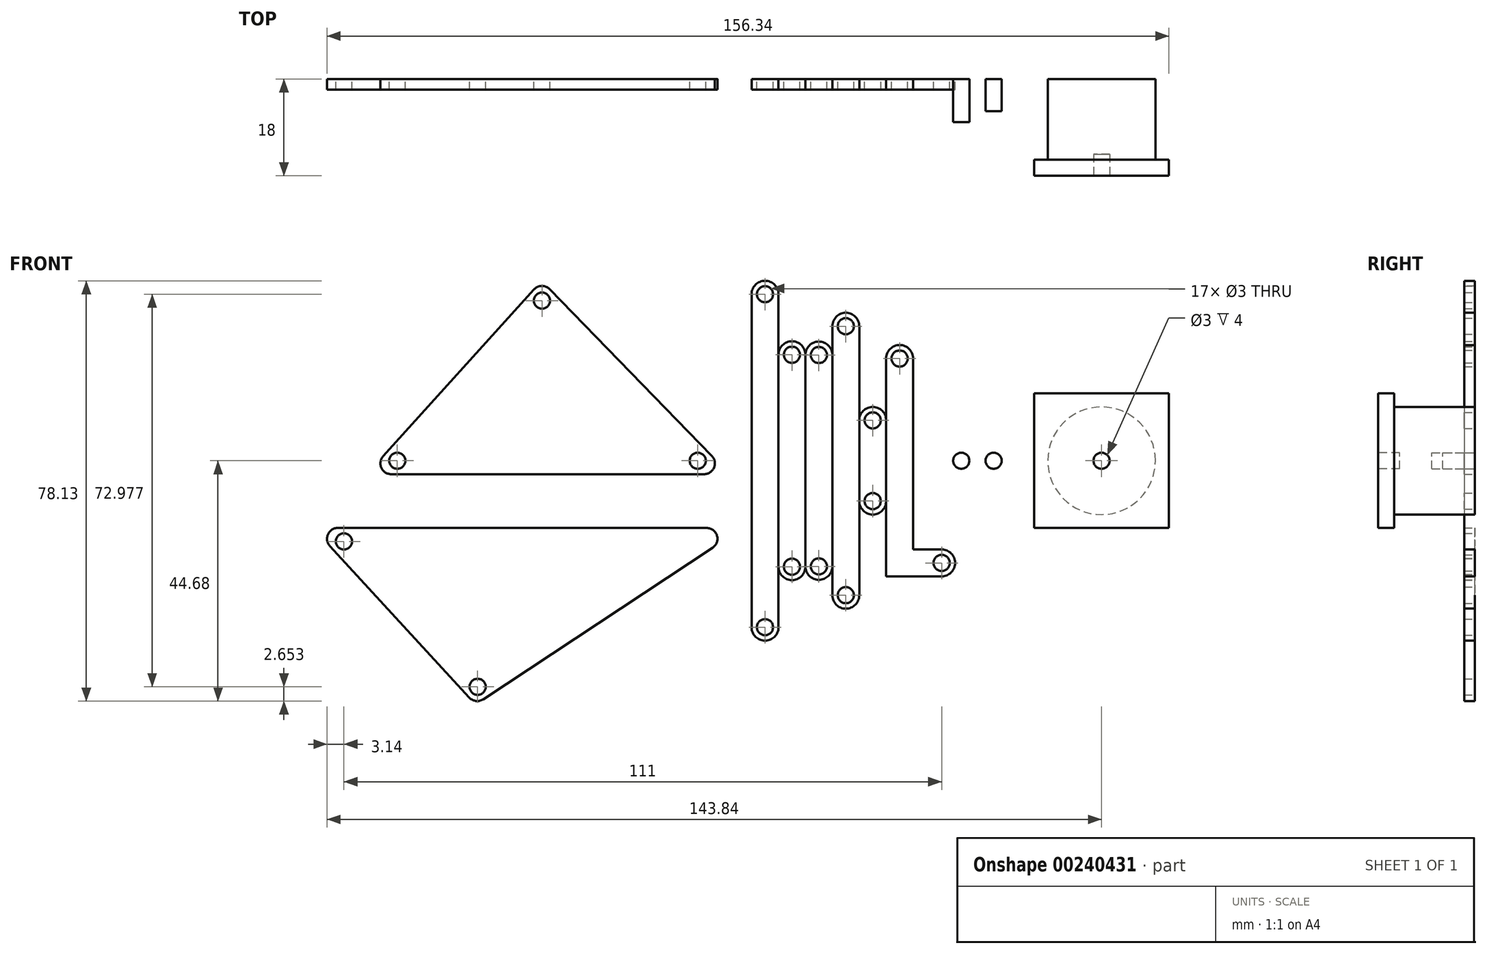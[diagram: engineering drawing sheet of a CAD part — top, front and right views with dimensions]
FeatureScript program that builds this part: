
annotation { "Feature Type Name" : "Feature", "Feature Type Description" : "" }
export const myFeature = defineFeature(function(context is Context, id is Id, definition is map)
    precondition{}
    {
        {
            var Q0;
            Q0=qCreatedBy(makeId("Front.planeOp"),FACE);
            var sketch = newSketch(context, id + "F0", { "sketchPlane" : qUnion([Q0])});
            skLineSegment(sketch, "E0", {"start": v(0, 7.5) * mm, "end": v(0, -7.5) * mm});
            skLineSegment(sketch, "E1", {"start": v(5, 7.5) * mm, "end": v(5, -7.5) * mm});
            skArc(sketch, "E2", {"start": v(5, 7.5) * mm, "mid": v(2.5, 10) * mm, "end": v(0, 7.5) * mm});
            skArc(sketch, "E3", {"start": v(0, -7.5) * mm, "mid": v(2.5, -10) * mm, "end": v(5, -7.5) * mm});
            skCircle(sketch, "E4", {"center": v(2.5, 7.5) * mm, "radius": 1.5 * mm});
            skCircle(sketch, "E5", {"center": v(2.5, -7.5) * mm, "radius": 1.5 * mm});
            skSolve(sketch);
        }
        {
            var Q0;
            Q0=makeQuery(id+"F0.imprint","IMPRINT",FACE,{"disambiguationData":[TD([[makeQuery(id+"F0.imprint","IMPRINT",EDGE,{"derivedFrom":sQuery(id+"F0.wireOp",EDGE,"E0")}),1.0]])]});
            extrude(context, id + "F1", {"entities" : qUnion([Q0]), "depth" : 2 * mm});
        }
        {
            var Q0;
            Q0=qCreatedBy(makeId("Front.planeOp"),FACE);
            var sketch = newSketch(context, id + "F2", { "sketchPlane" : qUnion([Q0])});
            skLineSegment(sketch, "E6", {"start": v(0, 25) * mm, "end": v(0, -25) * mm});
            skLineSegment(sketch, "E7", {"start": v(-5, 25) * mm, "end": v(-5, -25) * mm});
            skArc(sketch, "E8", {"start": v(0, 25) * mm, "mid": v(-2.5, 27.5) * mm, "end": v(-5, 25) * mm});
            skArc(sketch, "E9", {"start": v(-5, -25) * mm, "mid": v(-2.5, -27.5) * mm, "end": v(0, -25) * mm});
            skCircle(sketch, "E10", {"center": v(-2.5, 25) * mm, "radius": 1.5 * mm});
            skCircle(sketch, "E11", {"center": v(-2.5, -25) * mm, "radius": 1.5 * mm});
            skSolve(sketch);
        }
        {
            var Q0;
            Q0=makeQuery(id+"F2.imprint","IMPRINT",FACE,{"disambiguationData":[TD([[makeQuery(id+"F2.imprint","IMPRINT",EDGE,{"derivedFrom":sQuery(id+"F2.wireOp",EDGE,"E6")}),-1.0]])]});
            extrude(context, id + "F3", {"entities" : qUnion([Q0]), "depth" : 2 * mm});
        }
        {
            var Q0;
            Q0=qCreatedBy(makeId("Front.planeOp"),FACE);
            var sketch = newSketch(context, id + "F4", { "sketchPlane" : qUnion([Q0])});
            skLineSegment(sketch, "E12", {"start": v(-5, 19.65) * mm, "end": v(-5, -19.65) * mm});
            skLineSegment(sketch, "E13", {"start": v(-10, 19.65) * mm, "end": v(-10, -19.65) * mm});
            skArc(sketch, "E14", {"start": v(-5, 19.65) * mm, "mid": v(-7.5, 22.15) * mm, "end": v(-10, 19.65) * mm});
            skArc(sketch, "E15", {"start": v(-10, -19.65) * mm, "mid": v(-7.5, -22.15) * mm, "end": v(-5, -19.65) * mm});
            skCircle(sketch, "E16", {"center": v(-7.5, 19.65) * mm, "radius": 1.5 * mm});
            skCircle(sketch, "E17", {"center": v(-7.5, -19.65) * mm, "radius": 1.5 * mm});
            skSolve(sketch);
        }
        {
            var Q0;
            Q0=makeQuery(id+"F4.imprint","IMPRINT",FACE,{"disambiguationData":[TD([[makeQuery(id+"F4.imprint","IMPRINT",EDGE,{"derivedFrom":sQuery(id+"F4.wireOp",EDGE,"E12")}),-1.0]])]});
            extrude(context, id + "F5", {"entities" : qUnion([Q0]), "depth" : 2 * mm});
        }
        {
            var Q0;
            Q0=qCreatedBy(makeId("Front.planeOp"),FACE);
            var sketch = newSketch(context, id + "F6", { "sketchPlane" : qUnion([Q0])});
            skLineSegment(sketch, "E18", {"start": v(-10, 19.7) * mm, "end": v(-10, -19.7) * mm});
            skLineSegment(sketch, "E19", {"start": v(-15, 19.7) * mm, "end": v(-15, -19.7) * mm});
            skArc(sketch, "E20", {"start": v(-10, 19.7) * mm, "mid": v(-12.5, 22.2) * mm, "end": v(-15, 19.7) * mm});
            skArc(sketch, "E21", {"start": v(-15, -19.7) * mm, "mid": v(-12.5, -22.2) * mm, "end": v(-10, -19.7) * mm});
            skCircle(sketch, "E22", {"center": v(-12.5, 19.7) * mm, "radius": 1.5 * mm});
            skCircle(sketch, "E23", {"center": v(-12.5, -19.7) * mm, "radius": 1.5 * mm});
            skSolve(sketch);
        }
        {
            var Q0;
            Q0=makeQuery(id+"F6.imprint","IMPRINT",FACE,{"disambiguationData":[TD([[makeQuery(id+"F6.imprint","IMPRINT",EDGE,{"derivedFrom":sQuery(id+"F6.wireOp",EDGE,"E18")}),-1.0]])]});
            extrude(context, id + "F7", {"entities" : qUnion([Q0]), "depth" : 2 * mm});
        }
        {
            var Q0;
            Q0=qCreatedBy(makeId("Front.planeOp"),FACE);
            var sketch = newSketch(context, id + "F8", { "sketchPlane" : qUnion([Q0])});
            skLineSegment(sketch, "E24", {"start": v(-20, 30.95) * mm, "end": v(-20, -30.95) * mm});
            skLineSegment(sketch, "E25", {"start": v(-15, 30.95) * mm, "end": v(-15, -30.95) * mm});
            skArc(sketch, "E26", {"start": v(-15, 30.95) * mm, "mid": v(-17.5, 33.45) * mm, "end": v(-20, 30.95) * mm});
            skArc(sketch, "E27", {"start": v(-20, -30.95) * mm, "mid": v(-17.5, -33.45) * mm, "end": v(-15, -30.95) * mm});
            skCircle(sketch, "E28", {"center": v(-17.5, -30.95) * mm, "radius": 1.5 * mm});
            skCircle(sketch, "E29", {"center": v(-17.5, 30.95) * mm, "radius": 1.5 * mm});
            skSolve(sketch);
        }
        {
            var Q0;
            Q0=makeQuery(id+"F8.imprint","IMPRINT",FACE,{"disambiguationData":[TD([[makeQuery(id+"F8.imprint","IMPRINT",EDGE,{"derivedFrom":sQuery(id+"F8.wireOp",EDGE,"E24")}),1.0]])]});
            extrude(context, id + "F9", {"entities" : qUnion([Q0]), "depth" : 2 * mm});
        }
        {
            var Q0;
            Q0=qCreatedBy(makeId("Front.planeOp"),FACE);
            var sketch = newSketch(context, id + "F10", { "sketchPlane" : qUnion([Q0])});
            skLineSegment(sketch, "E30", {"start": v(-58.92, 29.76) * mm, "end": v(-30, 0) * mm, "construction": true});
            skLineSegment(sketch, "E31", {"start": v(-30, 0) * mm, "end": v(-85.8, 0) * mm, "construction": true});
            skLineSegment(sketch, "E32", {"start": v(-85.8, 0) * mm, "end": v(-58.92, 29.76) * mm, "construction": true});
            skCircle(sketch, "E33", {"center": v(-85.8, 0) * mm, "radius": 1.5 * mm});
            skCircle(sketch, "E34", {"center": v(-30, 0) * mm, "radius": 1.5 * mm});
            skCircle(sketch, "E35", {"center": v(-58.92, 29.76) * mm, "radius": 1.5 * mm});
            skLineSegment(sketch, "E36", {"start": v(-91.43, -2.5) * mm, "end": v(-24.08, -2.5) * mm});
            skLineSegment(sketch, "E37", {"start": v(-59, 33.42) * mm, "end": v(-91.43, -2.5) * mm});
            skLineSegment(sketch, "E38", {"start": v(-59, 33.42) * mm, "end": v(-24.08, -2.5) * mm});
            skSolve(sketch);
        }
        {
            var Q0;
            Q0=makeQuery(id+"F10.imprint","IMPRINT",FACE,{"disambiguationData":[TD([[makeQuery(id+"F10.imprint","IMPRINT",EDGE,{"derivedFrom":sQuery(id+"F10.wireOp",EDGE,"E33")}),-1.0]])]});
            extrude(context, id + "F11", {"entities" : qUnion([Q0]), "depth" : 2 * mm});
        }
        {
            var Q0;
            Q0=makeQuery(id+"F11.opExtrude","SWEPT_EDGE",EDGE,{"disambiguationData":[OSD([sQuery(id+"F10.wireOp",EDGE,"E36"),sQuery(id+"F10.wireOp",EDGE,"E37")])]});
            var Q1;
            Q1=makeQuery(id+"F11.opExtrude","SWEPT_EDGE",EDGE,{"disambiguationData":[OSD([sQuery(id+"F10.wireOp",EDGE,"E36"),sQuery(id+"F10.wireOp",EDGE,"E38")])]});
            var Q2;
            Q2=makeQuery(id+"F11.opExtrude","SWEPT_EDGE",EDGE,{"disambiguationData":[OSD([sQuery(id+"F10.wireOp",EDGE,"E37"),sQuery(id+"F10.wireOp",EDGE,"E38")])]});
            fillet(context, id + "F12", {"entities" : qUnion([Q0, Q1, Q2]), "radius" : 2 * mm, "tangentPropagation" : true, "allowEdgeOverflow" : false});
        }
        {
            var Q0;
            Q0=qCreatedBy(makeId("Front.planeOp"),FACE);
            var sketch = newSketch(context, id + "F13", { "sketchPlane" : qUnion([Q0])});
            skLineSegment(sketch, "E39", {"start": v(-95.7, -15) * mm, "end": v(-30, -15) * mm, "construction": true});
            skLineSegment(sketch, "E40", {"start": v(-30, -15) * mm, "end": v(-70.87, -42.03) * mm, "construction": true});
            skLineSegment(sketch, "E41", {"start": v(-70.87, -42.03) * mm, "end": v(-95.7, -15) * mm, "construction": true});
            skCircle(sketch, "E42", {"center": v(-95.7, -15) * mm, "radius": 1.5 * mm});
            skCircle(sketch, "E43", {"center": v(-70.87, -42.03) * mm, "radius": 1.5 * mm});
            skLineSegment(sketch, "E44", {"start": v(-101.4, -12.5) * mm, "end": v(-21.69, -12.5) * mm});
            skLineSegment(sketch, "E45", {"start": v(-21.69, -12.5) * mm, "end": v(-71.27, -45.29) * mm});
            skLineSegment(sketch, "E46", {"start": v(-71.27, -45.29) * mm, "end": v(-101.4, -12.5) * mm});
            skSolve(sketch);
        }
        {
            var Q0;
            Q0=makeQuery(id+"F13.imprint","IMPRINT",FACE,{"disambiguationData":[TD([[makeQuery(id+"F13.imprint","IMPRINT",EDGE,{"derivedFrom":sQuery(id+"F13.wireOp",EDGE,"E42")}),-1.0]])]});
            extrude(context, id + "F14", {"entities" : qUnion([Q0]), "depth" : 2 * mm});
        }
        {
            var Q0;
            Q0=makeQuery(id+"F14.opExtrude","SWEPT_EDGE",EDGE,{"disambiguationData":[OSD([sQuery(id+"F13.wireOp",EDGE,"E44"),sQuery(id+"F13.wireOp",EDGE,"E46")])]});
            var Q1;
            Q1=makeQuery(id+"F14.opExtrude","SWEPT_EDGE",EDGE,{"disambiguationData":[OSD([sQuery(id+"F13.wireOp",EDGE,"E45"),sQuery(id+"F13.wireOp",EDGE,"E46")])]});
            var Q2;
            Q2=makeQuery(id+"F14.opExtrude","SWEPT_EDGE",EDGE,{"disambiguationData":[OSD([sQuery(id+"F13.wireOp",EDGE,"E44"),sQuery(id+"F13.wireOp",EDGE,"E45")])]});
            fillet(context, id + "F15", {"entities" : qUnion([Q0, Q1, Q2]), "radius" : 2 * mm, "tangentPropagation" : true, "allowEdgeOverflow" : false});
        }
        {
            var Q0;
            Q0=qCreatedBy(makeId("Front.planeOp"),FACE);
            var sketch = newSketch(context, id + "F16", { "sketchPlane" : qUnion([Q0])});
            skLineSegment(sketch, "E47", {"start": v(7.5, 19) * mm, "end": v(7.5, -19) * mm, "construction": true});
            skLineSegment(sketch, "E48", {"start": v(7.5, -19) * mm, "end": v(15.3, -19) * mm, "construction": true});
            skArc(sketch, "E49", {"start": v(10, 19) * mm, "mid": v(7.5, 21.5) * mm, "end": v(5, 19) * mm});
            skArc(sketch, "E50", {"start": v(15.3, -21.5) * mm, "mid": v(17.8, -19) * mm, "end": v(15.3, -16.5) * mm});
            skLineSegment(sketch, "E51", {"start": v(5, 19) * mm, "end": v(5, -21.5) * mm});
            skLineSegment(sketch, "E52", {"start": v(15.3, -21.5) * mm, "end": v(5, -21.5) * mm});
            skLineSegment(sketch, "E53", {"start": v(10, 19) * mm, "end": v(10, -16.5) * mm});
            skLineSegment(sketch, "E54", {"start": v(15.3, -16.5) * mm, "end": v(10, -16.5) * mm});
            skCircle(sketch, "E55", {"center": v(7.5, 19) * mm, "radius": 1.5 * mm});
            skCircle(sketch, "E56", {"center": v(15.3, -19) * mm, "radius": 1.5 * mm});
            skSolve(sketch);
        }
        {
            var Q0;
            Q0=makeQuery(id+"F16.imprint","IMPRINT",FACE,{"disambiguationData":[TD([[makeQuery(id+"F16.imprint","IMPRINT",EDGE,{"derivedFrom":sQuery(id+"F16.wireOp",EDGE,"E49")}),1.0]])]});
            extrude(context, id + "F17", {"entities" : qUnion([Q0]), "depth" : 2 * mm});
        }
        {
            var Q0;
            Q0=qCreatedBy(makeId("Front.planeOp"),FACE);
            var sketch = newSketch(context, id + "F18", { "sketchPlane" : qUnion([Q0])});
            skCircle(sketch, "E57", {"center": v(24.95, 0) * mm, "radius": 1.5 * mm});
            skSolve(sketch);
        }
        {
            var Q0;
            Q0=makeQuery(id+"F18.imprint","IMPRINT",FACE,{"disambiguationData":[TD([[makeQuery(id+"F18.imprint","IMPRINT",EDGE,{"derivedFrom":sQuery(id+"F18.wireOp",EDGE,"E57")}),1.0]])]});
            extrude(context, id + "F19", {"entities" : qUnion([Q0]), "depth" : 6 * mm});
        }
        {
            var Q0;
            Q0=qCreatedBy(makeId("Front.planeOp"),FACE);
            var sketch = newSketch(context, id + "F20", { "sketchPlane" : qUnion([Q0])});
            skCircle(sketch, "E58", {"center": v(45, 0) * mm, "radius": 10 * mm});
            skSolve(sketch);
        }
        {
            var Q0;
            Q0=makeQuery(id+"F20.imprint","IMPRINT",FACE,{"disambiguationData":[TD([[makeQuery(id+"F20.imprint","IMPRINT",EDGE,{"derivedFrom":sQuery(id+"F20.wireOp",EDGE,"E58")}),1.0]])]});
            extrude(context, id + "F21", {"entities" : qUnion([Q0]), "depth" : 15 * mm});
        }
        {
            var Q0;
            Q0=makeQuery(id+"F21.opExtrude","CAP_FACE",FACE,{"disambiguationData":[OSD([sQuery(id+"F20.wireOp",EDGE,"E58")])],"isStart":false});
            var sketch = newSketch(context, id + "F22", { "sketchPlane" : qUnion([Q0])});
            skLineSegment(sketch, "E59.bottom", {"start": v(32.5, 12.5) * mm, "end": v(57.5, 12.5) * mm});
            skLineSegment(sketch, "E59.top", {"start": v(32.5, -12.5) * mm, "end": v(57.5, -12.5) * mm});
            skLineSegment(sketch, "E59.left", {"start": v(32.5, 12.5) * mm, "end": v(32.5, -12.5) * mm});
            skLineSegment(sketch, "E59.right", {"start": v(57.5, 12.5) * mm, "end": v(57.5, -12.5) * mm});
            skSolve(sketch);
        }
        {
            var Q0;
            Q0=makeQuery(id+"F22.imprint","IMPRINT",FACE,{"disambiguationData":[TD([[makeQuery(id+"F22.imprint","IMPRINT",EDGE,{"derivedFrom":sQuery(id+"F22.wireOp",EDGE,"E59.bottom")}),-1.0]])]});
            var Q1;
            Q1=makeQuery(id+"F22.imprint","IMPRINT",FACE,{"disambiguationData":[TD([[makeQuery(id+"F22.imprint","IMPRINT",EDGE,{"derivedFrom":makeQuery(id+"F21.opExtrude","CAP_EDGE",EDGE,{"disambiguationData":[OSD([sQuery(id+"F20.wireOp",EDGE,"E58")])],"isStart":false})}),1.0]])]});
            extrude(context, id + "F23", {"entities" : qUnion([Q0, Q1]), "operationType" : NewBodyOperationType.ADD, "depth" : 3 * mm});
        }
        {
            var Q0;
            Q0=makeQuery(id+"F23.opExtrude","CAP_FACE",FACE,{"disambiguationData":[OSD([sQuery(id+"F22.wireOp",EDGE,"E59.bottom"),sQuery(id+"F22.wireOp",EDGE,"E59.top"),sQuery(id+"F22.wireOp",EDGE,"E59.left"),sQuery(id+"F22.wireOp",EDGE,"E59.right")])],"isStart":false});
            var sketch = newSketch(context, id + "F24", { "sketchPlane" : qUnion([Q0])});
            skCircle(sketch, "E60", {"center": v(45, 0) * mm, "radius": 1.5 * mm});
            skSolve(sketch);
        }
        {
            var Q0;
            Q0=makeQuery(id+"F24.imprint","IMPRINT",FACE,{"disambiguationData":[TD([[makeQuery(id+"F24.imprint","IMPRINT",EDGE,{"derivedFrom":sQuery(id+"F24.wireOp",EDGE,"E60")}),1.0]])]});
            extrude(context, id + "F25", {"entities" : qUnion([Q0]), "operationType" : NewBodyOperationType.REMOVE, "oppositeDirection" : true, "depth" : 4 * mm});
        }
        {
            var Q0;
            Q0=qCreatedBy(makeId("Front.planeOp"),FACE);
            var sketch = newSketch(context, id + "F26", { "sketchPlane" : qUnion([Q0])});
            skCircle(sketch, "E61", {"center": v(18.95, 0) * mm, "radius": 1.5 * mm});
            skSolve(sketch);
        }
        {
            var Q0;
            Q0=makeQuery(id+"F26.imprint","IMPRINT",FACE,{"disambiguationData":[TD([[makeQuery(id+"F26.imprint","IMPRINT",EDGE,{"derivedFrom":sQuery(id+"F26.wireOp",EDGE,"E61")}),1.0]])]});
            extrude(context, id + "F27", {"entities" : qUnion([Q0]), "depth" : 8 * mm});
        }
    });
